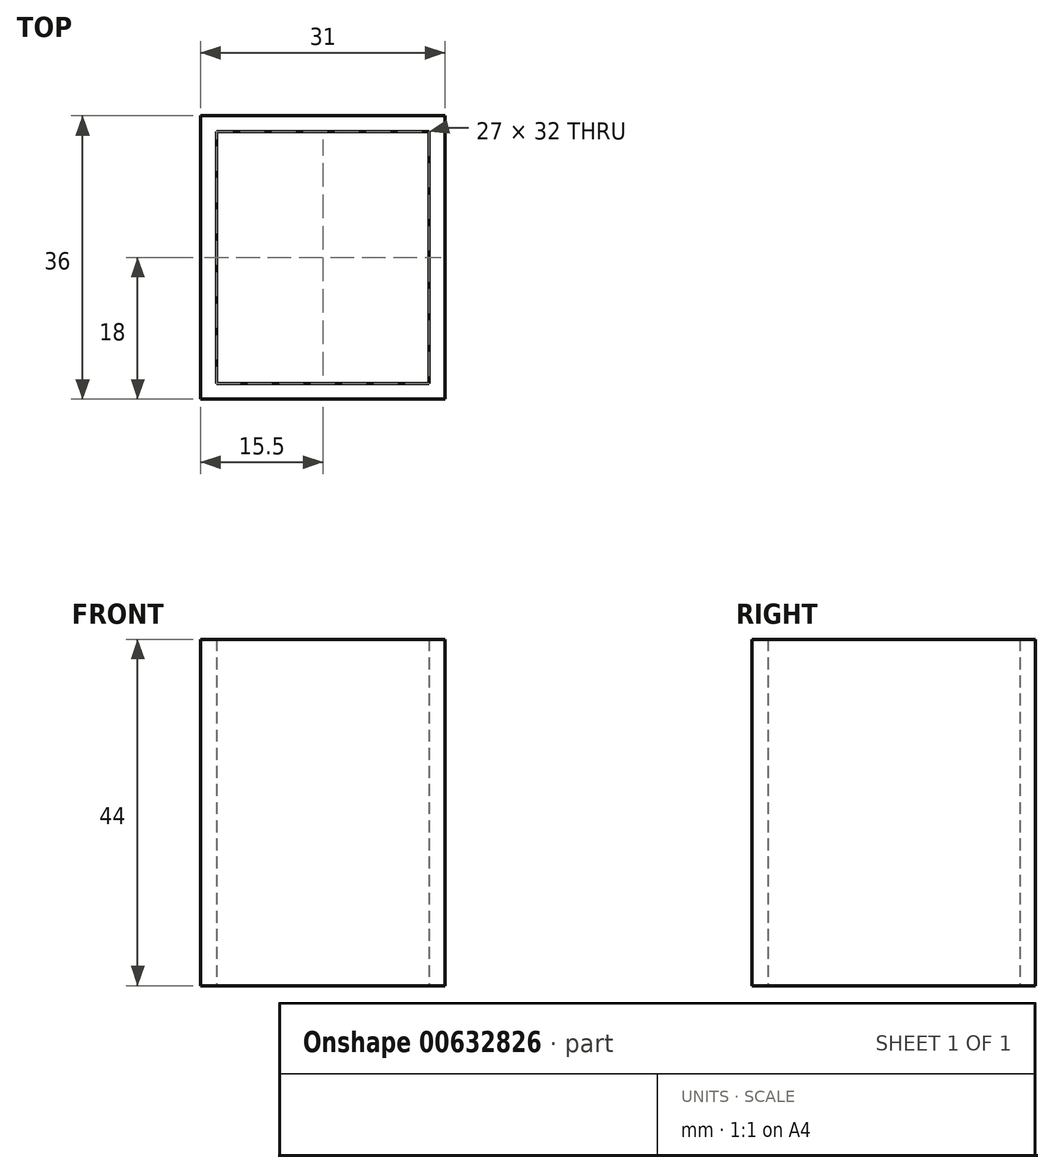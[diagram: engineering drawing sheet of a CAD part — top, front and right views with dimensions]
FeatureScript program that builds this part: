
annotation { "Feature Type Name" : "Feature", "Feature Type Description" : "" }
export const myFeature = defineFeature(function(context is Context, id is Id, definition is map)
    precondition{}
    {
        {
            var Q0;
            Q0=qCreatedBy(makeId("Top.planeOp"),FACE);
            var sketch = newSketch(context, id + "F0", { "sketchPlane" : qUnion([Q0])});
            skLineSegment(sketch, "E0.bottom", {"start": v(13.5, -16) * mm, "end": v(-13.5, -16) * mm});
            skLineSegment(sketch, "E0.top", {"start": v(13.5, 16) * mm, "end": v(-13.5, 16) * mm});
            skLineSegment(sketch, "E0.left", {"start": v(13.5, -16) * mm, "end": v(13.5, 16) * mm});
            skLineSegment(sketch, "E0.right", {"start": v(-13.5, -16) * mm, "end": v(-13.5, 16) * mm});
            skPoint(sketch, "E0.middle", {"position": v(0, 0) * mm});
            skLineSegment(sketch, "E1.bottom", {"start": v(15.5, -18) * mm, "end": v(-15.5, -18) * mm});
            skLineSegment(sketch, "E1.top", {"start": v(15.5, 18) * mm, "end": v(-15.5, 18) * mm});
            skLineSegment(sketch, "E1.left", {"start": v(15.5, -18) * mm, "end": v(15.5, 18) * mm});
            skLineSegment(sketch, "E1.right", {"start": v(-15.5, -18) * mm, "end": v(-15.5, 18) * mm});
            skSolve(sketch);
        }
        {
            var Q0;
            Q0=makeQuery(id+"F0.imprint","IMPRINT",FACE,{"disambiguationData":[TD([[makeQuery(id+"F0.imprint","IMPRINT",EDGE,{"derivedFrom":sQuery(id+"F0.wireOp",EDGE,"E0.bottom")}),1.0]])]});
            extrude(context, id + "F1", {"entities" : qUnion([Q0]), "depth" : 44 * mm, "offsetDistance" : 25 * mm});
        }
    });
